# Revit family: Bollard-1_800_Bollards-Low_Speed-Internal_Locking_Removable-CS3
name_source: partatom
category: Site
revit_build: Autodesk Revit 2017 (Build: 20160225_1515(x64)
units: mm (PartAtom-declared; Revit-internal decimal feet)

## family parameters
Always vertical = Yes
Cut with Voids When Loaded = No
OmniClass Number = 23.15.10.11.21
OmniClass Title = Traffic Safety Barriers and Protections
Part Type = Normal
Round Connector Dimension = Use Diameter
Shared = No
Work Plane-Based = No

## types (3) — shared parameters
Carbon Steel = No
Concrete Finish by others = Concrete, Lightweight
Concrete by others = Yes
Description = Stainless Steel Low Speed Removable Bollard
Finish = Metal-1_800_Bollards-Stainless_Steel
Foundation Depth = 3' - 0"
Foundation Width = 2' - 0"
Height = 3' - 0"
Height Below Grade = 1' - 5 1/4"
Manufacturer = 1-800-BOLLARDS
Model = Internal Locking Removable Low Speed Crash Tested Bollard
Product Documentation Link = https://1800bollards.com
Product Name = Low Speed Crash Tested Bollards
Product Page URL = https://1800bollards.com
Rebar by others = Yes
Stainless Steel = Yes
URL = https://1800bollards.com

## per-type parameters (varying)
| type | 4 in Bollard | 6 in Bollard | 8 in Bollard | Assembly Code | Bollard Cap Radius | Bollard Radius | Dome Height | Foundation Length | Thickness | Type Comments |
| 6 in 20 mph | No | Yes | No | G2020400 | 0' - 5 5/32" | 0' - 3 5/16" | 0' - 1 29/32" | 8' - 0" | 0' - 6 5/8" | 6 in 20 mph Low Speed Crash Tested Bollard |
| 4 in 10 mph | Yes | No | No | G2020400 | 0' - 4 3/32" | 0' - 2 1/4" | 0' - 1 5/16" | 5' - 0" | 0' - 4 1/2" | 4 in 10 mph Low Speed Crash Tested Bollard |
| 8 in 30 mph | No | No | Yes | G2010400 | 0' - 6 5/32" | 0' - 4 5/16" | 0' - 2 1/2" | 8' - 0" | 0' - 8 5/8" | 8 in 30 mph Low Speed Crash Tested Bollard |

## geometry (parser evidence)
native form markers: Sweep x5
no freeform markers — native parametric forms only
